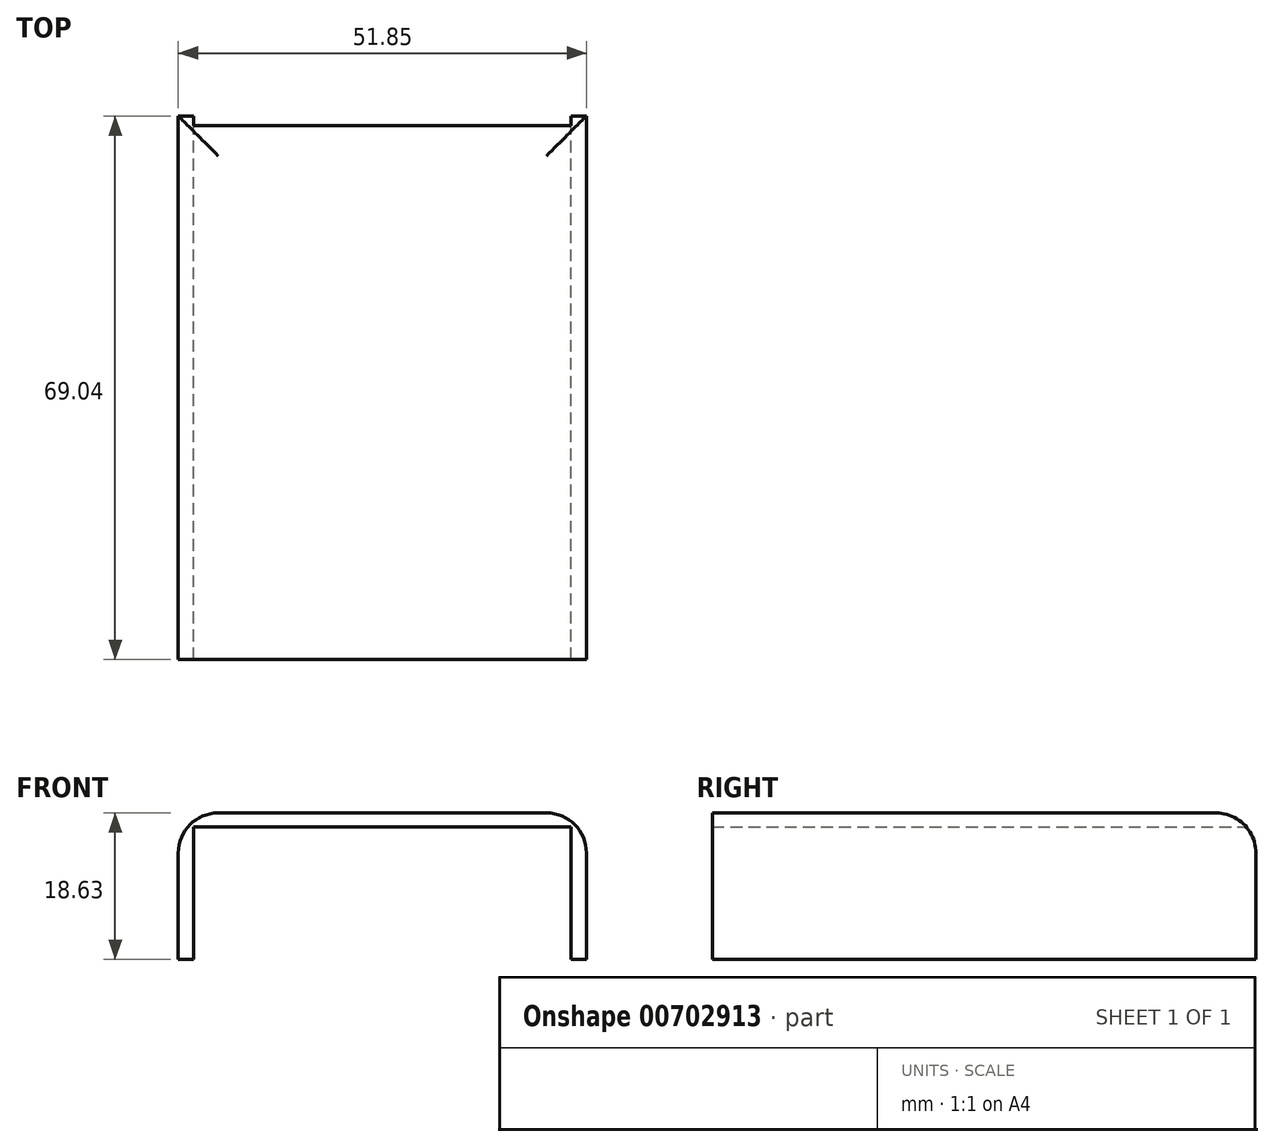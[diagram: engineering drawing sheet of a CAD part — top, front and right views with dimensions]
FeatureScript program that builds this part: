
annotation { "Feature Type Name" : "Feature", "Feature Type Description" : "" }
export const myFeature = defineFeature(function(context is Context, id is Id, definition is map)
    precondition{}
    {
        {
            var Q0;
            Q0=qCreatedBy(makeId("Front.planeOp"),FACE);
            var sketch = newSketch(context, id + "F0", { "sketchPlane" : qUnion([Q0])});
            skLineSegment(sketch, "E0.bottom", {"start": v(-30.27, 18.63) * mm, "end": v(21.58, 18.63) * mm});
            skLineSegment(sketch, "E0.left", {"start": v(-30.27, 18.63) * mm, "end": v(-30.27, 0) * mm});
            skLineSegment(sketch, "E0.right", {"start": v(21.58, 18.63) * mm, "end": v(21.58, 0) * mm});
            skPoint(sketch, "E0.middle", {"position": v(0, 0) * mm});
            skLineSegment(sketch, "E1.trimOffspring", {"start": v(21.58, 0) * mm, "end": v(21.6, 0) * mm});
            skLineSegment(sketch, "E2.bottom", {"start": v(-28.3, 16.88) * mm, "end": v(19.61, 16.88) * mm});
            skLineSegment(sketch, "E2.left", {"start": v(-28.3, 16.88) * mm, "end": v(-28.3, 0) * mm});
            skLineSegment(sketch, "E2.right", {"start": v(19.61, 16.88) * mm, "end": v(19.61, 0) * mm});
            skLineSegment(sketch, "E3", {"start": v(-30.27, 0) * mm, "end": v(-28.3, 0) * mm});
            skLineSegment(sketch, "E4", {"start": v(19.61, 0) * mm, "end": v(21.6, 0) * mm});
            skSolve(sketch);
        }
        {
            var Q0;
            Q0 = qSketchRegion(id + "F0", true);
            extrude(context, id + "F1", {"entities" : qUnion([Q0]), "endBound" : BoundingType.SYMMETRIC, "depth" : 69.05 * mm, "offsetDistance" : 25.4 * mm});
        }
        {
            var Q0;
            Q0=makeQuery(id+"F1.opExtrude","SWEPT_EDGE",EDGE,{"disambiguationData":[OSD([sQuery(id+"F0.wireOp",EDGE,"E0.bottom"),sQuery(id+"F0.wireOp",EDGE,"E0.left")])]});
            var Q1;
            Q1=makeQuery(id+"F1.opExtrude","CAP_EDGE",EDGE,{"disambiguationData":[OSD([sQuery(id+"F0.wireOp",EDGE,"E0.bottom")])],"isStart":true});
            var Q2;
            Q2=makeQuery(id+"F1.opExtrude","SWEPT_EDGE",EDGE,{"disambiguationData":[OSD([sQuery(id+"F0.wireOp",EDGE,"E0.bottom"),sQuery(id+"F0.wireOp",EDGE,"E0.right")])]});
            fillet(context, id + "F2", {"entities" : qUnion([Q0, Q1, Q2]), "radius" : 5.08 * mm, "tangentPropagation" : true, "allowEdgeOverflow" : false});
        }
    });
